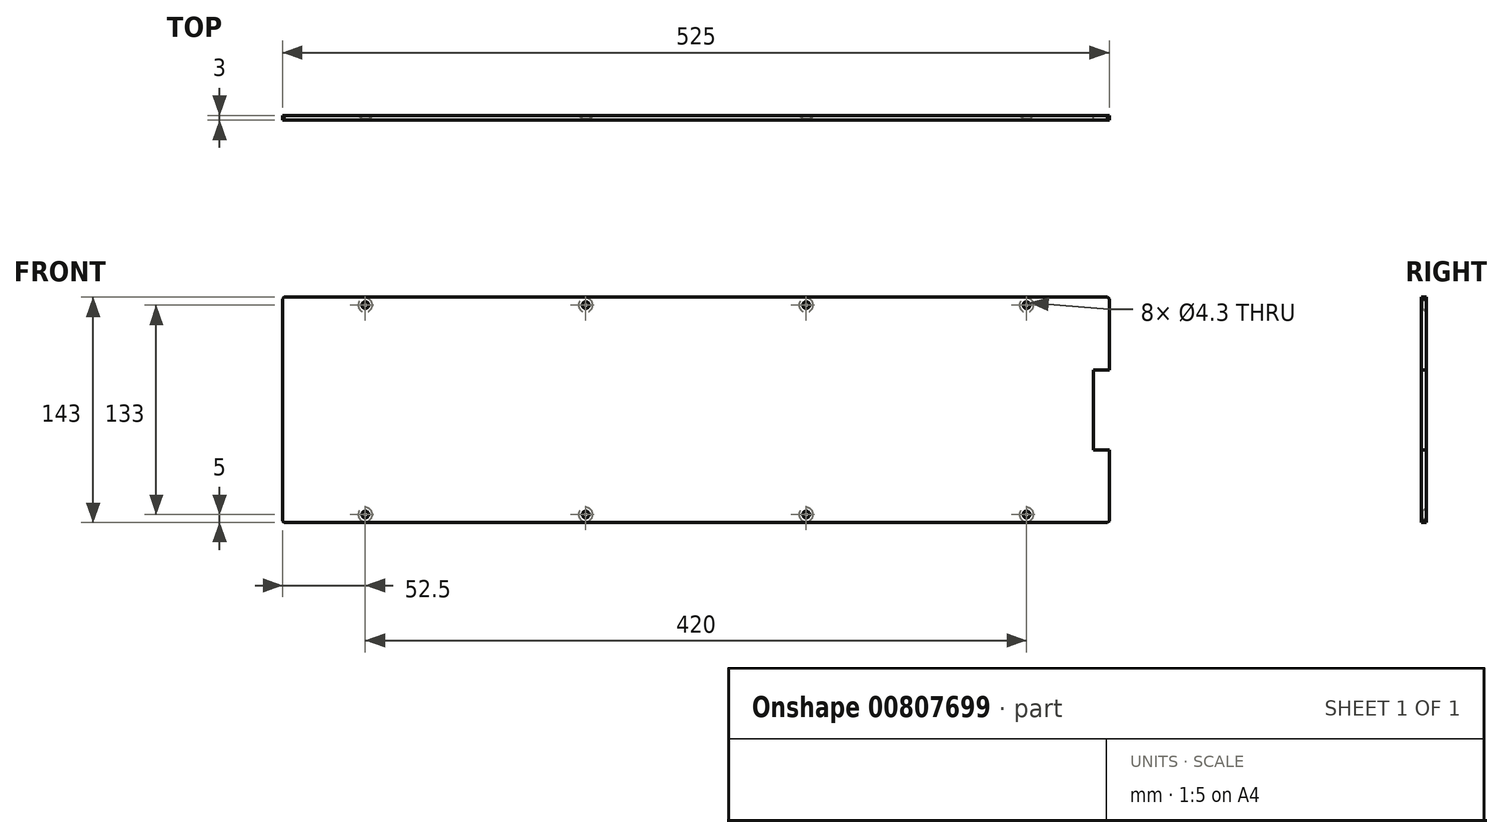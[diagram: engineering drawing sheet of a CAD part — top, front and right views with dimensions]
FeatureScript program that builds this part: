
annotation { "Feature Type Name" : "Feature", "Feature Type Description" : "" }
export const myFeature = defineFeature(function(context is Context, id is Id, definition is map)
    precondition{}
    {
        {
            var Q0;
            Q0=qCreatedBy(makeId("Front.planeOp"),FACE);
            var sketch = newSketch(context, id + "F0", { "sketchPlane" : qUnion([Q0])});
            skLineSegment(sketch, "E0", {"start": v(0, 0) * mm, "end": v(-525, 0) * mm});
            skLineSegment(sketch, "E1", {"start": v(-525, 0) * mm, "end": v(-525, -143) * mm});
            skLineSegment(sketch, "E2", {"start": v(-525, -143) * mm, "end": v(0, -143) * mm});
            skLineSegment(sketch, "E3", {"start": v(0, -143) * mm, "end": v(0, -96.9) * mm});
            skLineSegment(sketch, "E4", {"start": v(0, -96.9) * mm, "end": v(-10, -96.9) * mm});
            skLineSegment(sketch, "E5", {"start": v(-10, -96.9) * mm, "end": v(-10, -46.1) * mm});
            skLineSegment(sketch, "E6", {"start": v(-10, -46.1) * mm, "end": v(0, -46.1) * mm});
            skLineSegment(sketch, "E7", {"start": v(0, -46.1) * mm, "end": v(0, 0) * mm});
            skSolve(sketch);
        }
        {
            var Q0;
            Q0 = qSketchRegion(id + "F0", true);
            extrude(context, id + "F1", {"entities" : qUnion([Q0]), "depth" : 3 * mm, "offsetDistance" : 25 * mm});
        }
        {
            var Q0;
            Q0=qCreatedBy(makeId("Front.planeOp"),FACE);
            var sketch = newSketch(context, id + "F2", { "sketchPlane" : qUnion([Q0])});
            skPoint(sketch, "E8", {"position": v(-472.5, -138) * mm});
            skPoint(sketch, "E9", {"position": v(-192.5, -138) * mm});
            skPoint(sketch, "E10", {"position": v(-332.5, -138) * mm});
            skPoint(sketch, "E11", {"position": v(-52.5, -138) * mm});
            skPoint(sketch, "E12", {"position": v(-52.5, -5) * mm});
            skPoint(sketch, "E13", {"position": v(-332.5, -5) * mm});
            skPoint(sketch, "E14", {"position": v(-192.5, -5) * mm});
            skPoint(sketch, "E15", {"position": v(-472.5, -5) * mm});
            skSolve(sketch);
        }
        {
            var Q0;
            Q0=sQuery(id+"F2.wireOp",VERTEX,"422321d4-ebc9-4960-9ce4-a9f705f8aa04");
            var Q1;
            Q1=sQuery(id+"F2.wireOp",VERTEX,"E15");
            var Q2;
            Q2=sQuery(id+"F2.wireOp",VERTEX,"E13");
            var Q3;
            Q3=sQuery(id+"F2.wireOp",VERTEX,"E14");
            var Q4;
            Q4=sQuery(id+"F2.wireOp",VERTEX,"E12");
            var Q5;
            Q5=sQuery(id+"F2.wireOp",VERTEX,"b59c22aa-edf1-47ce-b889-e012d4324ee3");
            var Q6;
            Q6=sQuery(id+"F2.wireOp",VERTEX,"f5eac521-7d33-44cc-93ff-620413ee59f5");
            var Q7;
            Q7=sQuery(id+"F2.wireOp",VERTEX,"E11");
            var Q8;
            Q8=sQuery(id+"F2.wireOp",VERTEX,"E9");
            var Q9;
            Q9=sQuery(id+"F2.wireOp",VERTEX,"E10");
            var Q10;
            Q10=sQuery(id+"F2.wireOp",VERTEX,"E8");
            var Q11;
            Q11=sQuery(id+"F2.wireOp",VERTEX,"93c23eff-6332-40c2-ba3d-1e38b10ba658");
            var Q12;
            Q12=makeQuery(id+"F1.opExtrude","SWEPT_BODY",BODY,{"disambiguationData":[OSD([sQuery(id+"F0.wireOp",EDGE,"E0"),sQuery(id+"F0.wireOp",EDGE,"E1"),sQuery(id+"F0.wireOp",EDGE,"E2"),sQuery(id+"F0.wireOp",EDGE,"E3"),sQuery(id+"F0.wireOp",EDGE,"E4"),sQuery(id+"F0.wireOp",EDGE,"E5"),sQuery(id+"F0.wireOp",EDGE,"E6"),sQuery(id+"F0.wireOp",EDGE,"E7")])]});
            hole(context, id + "F3", {"style" : HoleStyle.C_SINK, "endStyle" : HoleEndStyle.THROUGH, "oppositeDirection" : true, "holeDiameter" : 4.3 * mm, "cSinkDiameter" : 9 * mm, "cSinkAngle" : 90 * degree, "majorDiameter" : 5 * mm, "tappedDepth" : 20 * mm, "tapClearance" : 3, "locations" : qUnion([Q0, Q1, Q2, Q3, Q4, Q5, Q6, Q7, Q8, Q9, Q10, Q11]), "scope" : qUnion([Q12]), "startStyle" : HoleStartStyle.PART});
        }
        {
            var Q0;
            Q0=makeQuery(id+"F1.opExtrude","SWEPT_EDGE",EDGE,{"disambiguationData":[OSD([sQuery(id+"F0.wireOp",EDGE,"E0"),sQuery(id+"F0.wireOp",EDGE,"E1")])]});
            var Q1;
            Q1=makeQuery(id+"F1.opExtrude","SWEPT_EDGE",EDGE,{"disambiguationData":[OSD([sQuery(id+"F0.wireOp",EDGE,"E1"),sQuery(id+"F0.wireOp",EDGE,"E2")])]});
            var Q2;
            Q2=makeQuery(id+"F1.opExtrude","SWEPT_EDGE",EDGE,{"disambiguationData":[OSD([sQuery(id+"F0.wireOp",EDGE,"E2"),sQuery(id+"F0.wireOp",EDGE,"E3")])]});
            var Q3;
            Q3=makeQuery(id+"F1.opExtrude","SWEPT_EDGE",EDGE,{"disambiguationData":[OSD([sQuery(id+"F0.wireOp",EDGE,"E0"),sQuery(id+"F0.wireOp",EDGE,"E7")])]});
            chamfer(context, id + "F4", {"entities" : qUnion([Q0, Q1, Q2, Q3]), "width" : 1 * mm, "tangentPropagation" : true});
        }
    });
